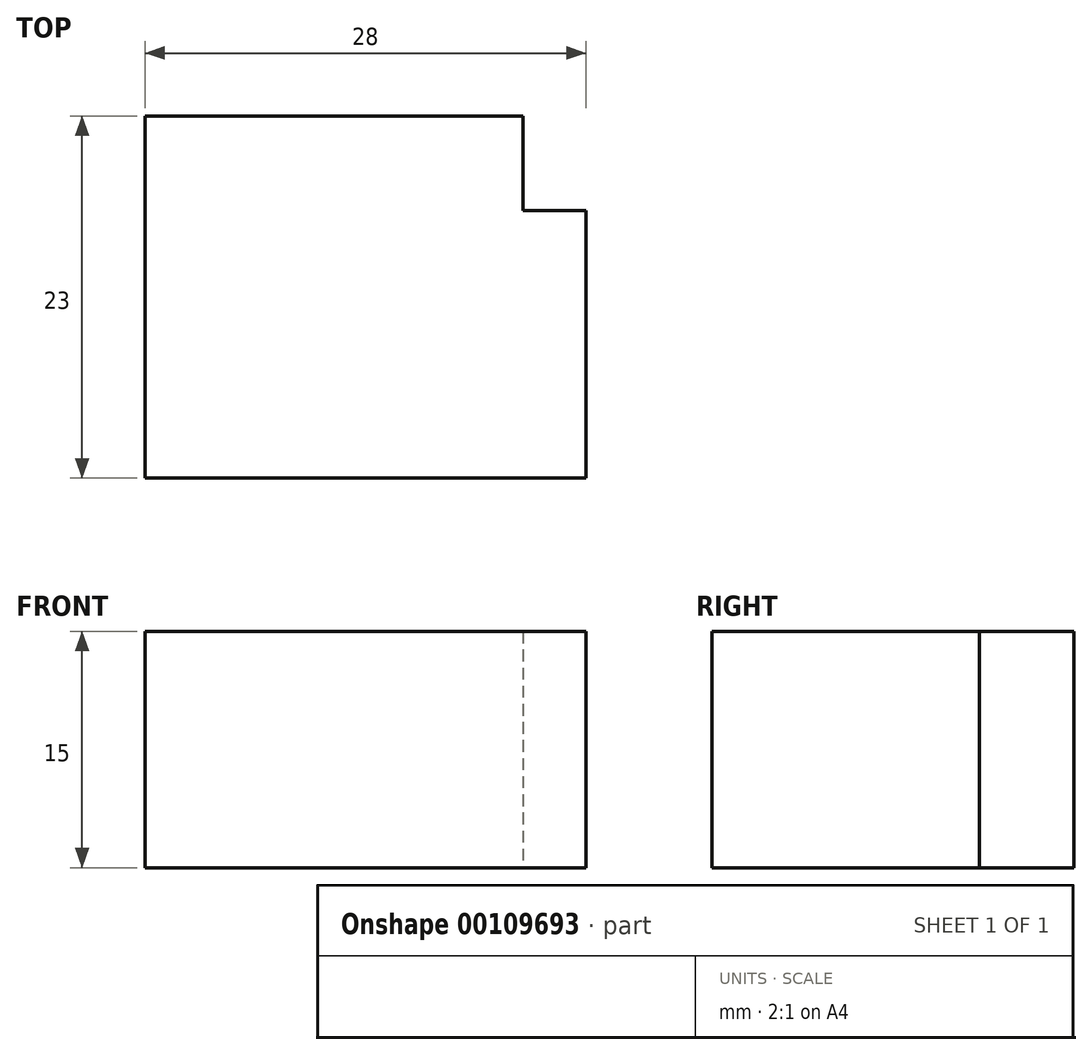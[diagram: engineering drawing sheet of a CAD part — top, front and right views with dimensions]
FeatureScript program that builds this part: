
annotation { "Feature Type Name" : "Feature", "Feature Type Description" : "" }
export const myFeature = defineFeature(function(context is Context, id is Id, definition is map)
    precondition{}
    {
        {
            var Q0;
            Q0=qCreatedBy(makeId("Top.planeOp"),FACE);
            var sketch = newSketch(context, id + "F0", { "sketchPlane" : qUnion([Q0])});
            skLineSegment(sketch, "E0", {"start": v(0, 0) * mm, "end": v(28, 0) * mm});
            skLineSegment(sketch, "E1", {"start": v(0, 0) * mm, "end": v(0, 23) * mm});
            skLineSegment(sketch, "E2", {"start": v(0, 23) * mm, "end": v(24, 23) * mm});
            skLineSegment(sketch, "E3", {"start": v(28, 0) * mm, "end": v(28, 17) * mm});
            skLineSegment(sketch, "E4", {"start": v(24, 23) * mm, "end": v(24, 17) * mm});
            skLineSegment(sketch, "E5", {"start": v(24, 17) * mm, "end": v(28, 17) * mm});
            skSolve(sketch);
        }
        {
            var Q0;
            Q0 = qSketchRegion(id + "F0", true);
            extrude(context, id + "F1", {"entities" : qUnion([Q0]), "depth" : 15 * mm});
        }
    });
